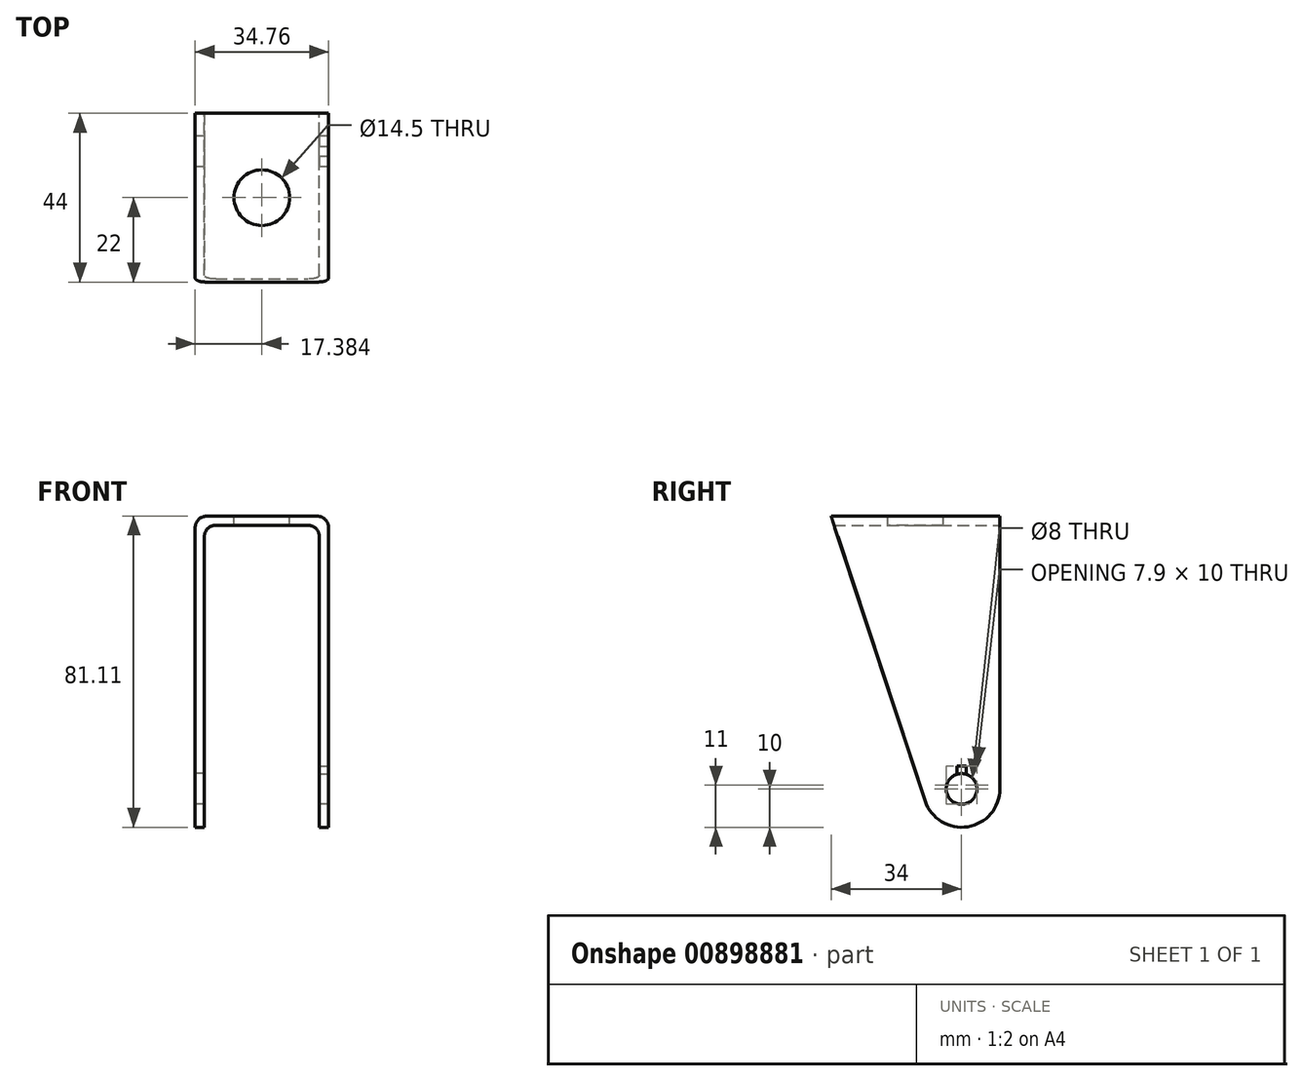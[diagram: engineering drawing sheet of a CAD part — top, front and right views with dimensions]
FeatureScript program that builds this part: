
annotation { "Feature Type Name" : "Feature", "Feature Type Description" : "" }
export const myFeature = defineFeature(function(context is Context, id is Id, definition is map)
    precondition{}
    {
        {
            var Q0;
            Q0=qCreatedBy(makeId("Front.planeOp"),FACE);
            var sketch = newSketch(context, id + "F0", { "sketchPlane" : qUnion([Q0])});
            skLineSegment(sketch, "E0", {"start": v(-81.56, 0) * mm, "end": v(-81.56, 81.1) * mm});
            skLineSegment(sketch, "E1", {"start": v(-81.56, 81.1) * mm, "end": v(-46.8, 81.1) * mm});
            skLineSegment(sketch, "E2", {"start": v(-46.8, 81.1) * mm, "end": v(-46.8, 0) * mm});
            skLineSegment(sketch, "E3.0", {"start": v(-79.18, 0) * mm, "end": v(-79.18, 78.73) * mm});
            skLineSegment(sketch, "E4.0", {"start": v(-49.18, 78.73) * mm, "end": v(-49.18, 0) * mm});
            skLineSegment(sketch, "E5.0", {"start": v(-79.18, 78.73) * mm, "end": v(-49.18, 78.73) * mm});
            skLineSegment(sketch, "E6", {"start": v(-81.56, 0) * mm, "end": v(-79.18, 0) * mm});
            skLineSegment(sketch, "E7", {"start": v(-49.18, 0) * mm, "end": v(-46.8, 0) * mm});
            skSolve(sketch);
        }
        {
            var Q0;
            Q0 = qSketchRegion(id + "F0", true);
            extrude(context, id + "F1", {"entities" : qUnion([Q0]), "depth" : 44 * mm, "offsetDistance" : 25 * mm});
        }
        {
            var Q0;
            Q0=makeQuery(id+"F1.opExtrude","SWEPT_FACE",FACE,{"disambiguationData":[OSD([sQuery(id+"F0.wireOp",EDGE,"E2")])]});
            var sketch = newSketch(context, id + "F2", { "sketchPlane" : qUnion([Q0])});
            skArc(sketch, "E8", {"start": v(-19.5, 6.87) * mm, "mid": v(-7.28, 0.38) * mm, "end": v(-0.27, 12.3) * mm});
            skLineSegment(sketch, "E9", {"start": v(-44, 81.1) * mm, "end": v(-19.5, 6.87) * mm});
            skSolve(sketch);
        }
        {
            var Q0;
            {var subQ0=sQuery(id+"F2.wireOp",EDGE,"E9");Q0=makeQuery(id+"F2.imprint","IMPRINT",FACE,{"disambiguationData":[TD([[makeQuery(id+"F2.imprint","IMPRINT",EDGE,{"derivedFrom":subQ0}),-1.0]])]});}
            extrude(context, id + "F3", {"entities" : qUnion([Q0]), "operationType" : NewBodyOperationType.REMOVE, "oppositeDirection" : true, "depth" : 45.2 * mm, "offsetDistance" : 25 * mm});
        }
        {
            var Q0;
            {var subQ0=sQuery(id+"F2.wireOp",EDGE,"E8");var subQ1=sQuery(id+"F0.wireOp",EDGE,"E2");var subQ2=makeQuery(id+"F1.opExtrude","CAP_EDGE",EDGE,{"disambiguationData":[OSD([subQ1])],"isStart":true});var subQ3=makeQuery(id+"F2.imprint","INTERSECT",VERTEX,{"derivedFrom":[subQ2,subQ0]});Q0=makeQuery(id+"F2.imprint","IMPRINT",FACE,{"disambiguationData":[TD([[makeQuery(id+"F2.imprint","IMPRINT",EDGE,{"disambiguationData":[TD([[subQ3,1.0]])],"derivedFrom":subQ0}),-1.0]])]});}
            extrude(context, id + "F4", {"entities" : qUnion([Q0]), "operationType" : NewBodyOperationType.REMOVE, "oppositeDirection" : true, "depth" : 52 * mm, "offsetDistance" : 25 * mm});
        }
        {
            var Q0;
            Q0=makeQuery(id+"F1.opExtrude","SWEPT_FACE",FACE,{"disambiguationData":[OSD([sQuery(id+"F0.wireOp",EDGE,"E0")])]});
            var sketch = newSketch(context, id + "F5", { "sketchPlane" : qUnion([Q0])});
            skCircle(sketch, "E10", {"center": v(10, 10) * mm, "radius": 4 * mm});
            skSolve(sketch);
        }
        {
            var Q0;
            Q0 = qSketchRegion(id + "F5", true);
            extrude(context, id + "F6", {"entities" : qUnion([Q0]), "operationType" : NewBodyOperationType.REMOVE, "oppositeDirection" : true, "depth" : 57.3 * mm, "offsetDistance" : 25 * mm});
        }
        {
            var Q0;
            Q0=makeQuery(id+"F1.opExtrude","SWEPT_FACE",FACE,{"disambiguationData":[OSD([sQuery(id+"F0.wireOp",EDGE,"E1")])]});
            var sketch = newSketch(context, id + "F7", { "sketchPlane" : qUnion([Q0])});
            skPoint(sketch, "E11.endSnap0", {"position": v(-46.8, -22) * mm});
            skCircle(sketch, "E12", {"center": v(-64.18, -22) * mm, "radius": 7.25 * mm});
            skPoint(sketch, "E13.end.orphan", {"position": v(-81.56, -22) * mm});
            skPoint(sketch, "E13.start.orphan", {"position": v(-81.56, 0) * mm});
            skSolve(sketch);
        }
        {
            var Q0;
            Q0 = qSketchRegion(id + "F7", true);
            extrude(context, id + "F8", {"entities" : qUnion([Q0]), "operationType" : NewBodyOperationType.REMOVE, "oppositeDirection" : true, "depth" : 25 * mm, "offsetDistance" : 25 * mm});
        }
        {
            var Q0;
            Q0=makeQuery(id+"F1.opExtrude","SWEPT_EDGE",EDGE,{"disambiguationData":[OSD([sQuery(id+"F0.wireOp",EDGE,"E0"),sQuery(id+"F0.wireOp",EDGE,"E1")])]});
            fillet(context, id + "F9", {"entities" : qUnion([Q0]), "radius" : 3 * mm, "tangentPropagation" : true, "allowEdgeOverflow" : false});
        }
        {
            var Q0;
            Q0=makeQuery(id+"F1.opExtrude","SWEPT_EDGE",EDGE,{"disambiguationData":[OSD([sQuery(id+"F0.wireOp",EDGE,"E1"),sQuery(id+"F0.wireOp",EDGE,"E2")])]});
            fillet(context, id + "F10", {"entities" : qUnion([Q0]), "radius" : 3 * mm, "tangentPropagation" : true, "allowEdgeOverflow" : false});
        }
        {
            var Q0;
            Q0=makeQuery(id+"F1.opExtrude","SWEPT_EDGE",EDGE,{"disambiguationData":[OSD([sQuery(id+"F0.wireOp",EDGE,"E4.0"),sQuery(id+"F0.wireOp",EDGE,"E5.0")])]});
            fillet(context, id + "F11", {"entities" : qUnion([Q0]), "radius" : 3 * mm, "tangentPropagation" : true, "allowEdgeOverflow" : false});
        }
        {
            var Q0;
            Q0=makeQuery(id+"F1.opExtrude","SWEPT_EDGE",EDGE,{"disambiguationData":[OSD([sQuery(id+"F0.wireOp",EDGE,"E3.0"),sQuery(id+"F0.wireOp",EDGE,"E5.0")])]});
            fillet(context, id + "F12", {"entities" : qUnion([Q0]), "radius" : 3 * mm, "tangentPropagation" : true, "allowEdgeOverflow" : false});
        }
        {
            var Q0;
            {var subQ2=sQuery(id+"F2.wireOp",EDGE,"E9");Q0=makeQuery(id+"F2.imprint","IMPRINT",FACE,{"disambiguationData":[TD([[makeQuery(id+"F2.imprint","IMPRINT",EDGE,{"derivedFrom":subQ2}),1.0]])]});}
            var sketch = newSketch(context, id + "F13", { "sketchPlane" : qUnion([Q0])});
            skLineSegment(sketch, "E14", {"start": v(-10, 10) * mm, "end": v(-10, 14) * mm});
            skLineSegment(sketch, "E15", {"start": v(-11.25, 14) * mm, "end": v(-11.25, 16) * mm});
            skLineSegment(sketch, "E16", {"start": v(-8.75, 14) * mm, "end": v(-8.75, 16) * mm});
            skLineSegment(sketch, "E17", {"start": v(-11.25, 16) * mm, "end": v(-8.75, 16) * mm});
            skLineSegment(sketch, "E18", {"start": v(-8.75, 14) * mm, "end": v(-8.75, 13.57) * mm});
            skLineSegment(sketch, "E19", {"start": v(-8.75, 13.57) * mm, "end": v(-11.25, 13.5) * mm});
            skLineSegment(sketch, "E20", {"start": v(-11.25, 13.5) * mm, "end": v(-11.25, 14) * mm});
            skSolve(sketch);
        }
        {
            var Q0;
            Q0 = qSketchRegion(id + "F13", true);
            extrude(context, id + "F14", {"entities" : qUnion([Q0]), "operationType" : NewBodyOperationType.REMOVE, "oppositeDirection" : true, "depth" : 25 * mm, "offsetDistance" : 25 * mm});
        }
        {
            var Q0;
            Q0 = qSketchRegion(id + "F13", true);
            extrude(context, id + "F15", {"entities" : qUnion([Q0]), "operationType" : NewBodyOperationType.REMOVE, "oppositeDirection" : true, "depth" : 25 * mm, "offsetDistance" : 25 * mm});
        }
        {
            var Q0;
            {var subQ2=sQuery(id+"F2.wireOp",EDGE,"E9");Q0=makeQuery(id+"F2.imprint","IMPRINT",FACE,{"disambiguationData":[TD([[makeQuery(id+"F2.imprint","IMPRINT",EDGE,{"derivedFrom":subQ2}),1.0]])]});}
            var sketch = newSketch(context, id + "F16", { "sketchPlane" : qUnion([Q0])});
            skLineSegment(sketch, "E21", {"start": v(-8.75, 14.02) * mm, "end": v(-8.75, 13.35) * mm});
            skLineSegment(sketch, "E22", {"start": v(-11.25, 14.02) * mm, "end": v(-11.25, 13.35) * mm});
            skLineSegment(sketch, "E23", {"start": v(-8.75, 13.35) * mm, "end": v(-11.25, 13.35) * mm});
            skSolve(sketch);
        }
        {
            var Q0;
            Q0 = qSketchRegion(id + "F16", true);
            var Q1;
            Q1=makeQuery(id+"F5.imprint","IMPRINT",FACE,{"disambiguationData":[TD([[makeQuery(id+"F5.imprint","IMPRINT",EDGE,{"derivedFrom":sQuery(id+"F5.wireOp",EDGE,"E10")}),1.0]])]});
            extrude(context, id + "F17", {"entities" : qUnion([Q0, Q1]), "depth" : 25 * mm, "offsetDistance" : 25 * mm});
        }
        {
            var Q0;
            Q0 = qSketchRegion(id + "F13", true);
            extrude(context, id + "F18", {"entities" : qUnion([Q0]), "operationType" : NewBodyOperationType.REMOVE, "oppositeDirection" : true, "depth" : 25 * mm, "offsetDistance" : 25 * mm});
        }
        {
            var Q0;
            Q0=makeQuery(id+"F17.opExtrude","CAP_FACE",FACE,{"disambiguationData":[OSD([sQuery(id+"F5.wireOp",EDGE,"E10")])],"isStart":false});
            extrude(context, id + "F19", {"entities" : qUnion([Q0]), "operationType" : NewBodyOperationType.REMOVE, "oppositeDirection" : true, "depth" : 25 * mm, "offsetDistance" : 25 * mm});
        }
        {
            var Q0;
            {var subQ2=sQuery(id+"F2.wireOp",EDGE,"E9");Q0=makeQuery(id+"F2.imprint","IMPRINT",FACE,{"disambiguationData":[TD([[makeQuery(id+"F2.imprint","IMPRINT",EDGE,{"derivedFrom":subQ2}),1.0]])]});}
            var sketch = newSketch(context, id + "F20", { "sketchPlane" : qUnion([Q0])});
            skSolve(sketch);
        }
        {
            var Q0;
            Q0 = qSketchRegion(id + "F20", true);
            var Q1;
            Q1=makeQuery(id+"F13.imprint","IMPRINT",FACE,{"disambiguationData":[TD([[makeQuery(id+"F13.imprint","IMPRINT",EDGE,{"derivedFrom":sQuery(id+"F13.wireOp",EDGE,"E15")}),-1.0]])]});
            extrude(context, id + "F21", {"entities" : qUnion([Q0, Q1]), "operationType" : NewBodyOperationType.REMOVE, "oppositeDirection" : true, "depth" : 25 * mm, "offsetDistance" : 25 * mm});
        }
    });
